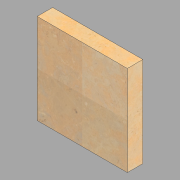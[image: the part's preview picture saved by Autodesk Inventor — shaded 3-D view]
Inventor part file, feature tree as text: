
AUTODESK INVENTOR PART (.ipt)
format: ipt  version: 2022.1 (Build 261234020, 234B)  size: 105,984 bytes
history: native  units: in
note: dims shown in document units (in); Inventor stores cm internally (conversion verified against a paired STEP export)
features: extrude x1, sketch x1
ambient origin geometry x8: Origin, YZ Plane, XZ Plane, XY Plane, X Axis, Y Axis, Z Axis, Center Point
bodies: Solid1 (feature_tree)
feature tree (2):
  extrude  "Extrusion1"  Depth=11.625in
  sketch  "Sketch1"  dims[d0=11.625in d1=11.625in d2=2.0in d3=0.0in]
